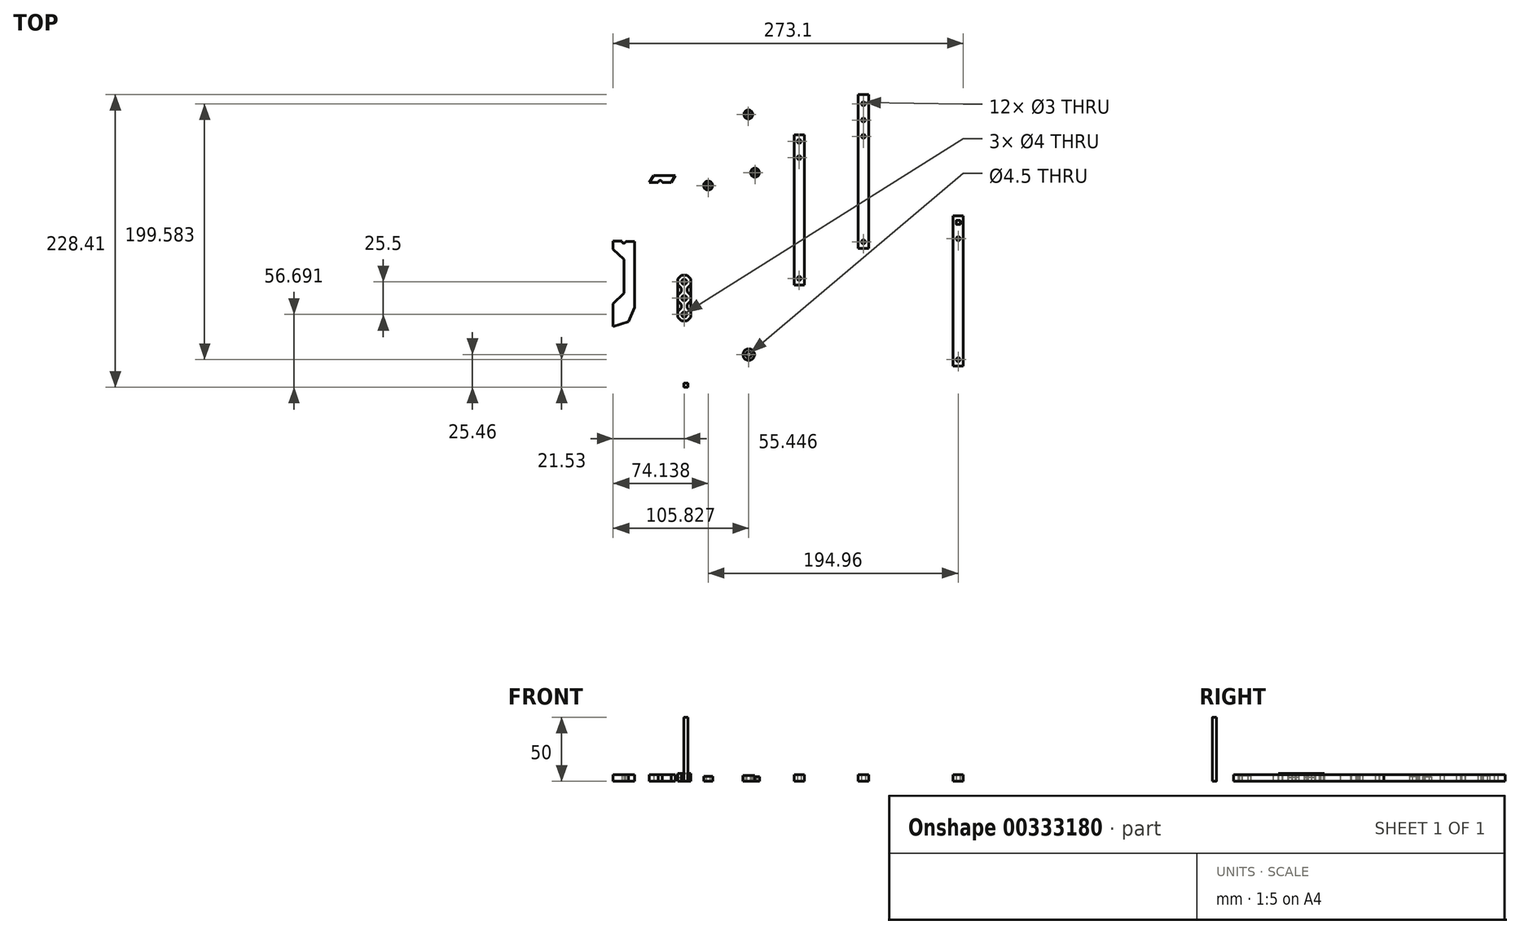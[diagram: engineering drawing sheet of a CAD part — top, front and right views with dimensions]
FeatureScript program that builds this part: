
annotation { "Feature Type Name" : "Feature", "Feature Type Description" : "" }
export const myFeature = defineFeature(function(context is Context, id is Id, definition is map)
    precondition{}
    {
        {
            var Q0;
            Q0=qCreatedBy(makeId("Top.planeOp"),FACE);
            var sketch = newSketch(context, id + "F0", { "sketchPlane" : qUnion([Q0])});
            skLineSegment(sketch, "E0", {"start": v(-67.95, 43.9) * mm, "end": v(-50.95, 43.9) * mm});
            skLineSegment(sketch, "E1", {"start": v(-67.95, 43.9) * mm, "end": v(-99.55, -7.1) * mm});
            skLineSegment(sketch, "E2", {"start": v(-50.95, 43.9) * mm, "end": v(-82.81, -7.53) * mm});
            skLineSegment(sketch, "E3", {"start": v(-99.55, -7.1) * mm, "end": v(-99.55, -13.4) * mm});
            skLineSegment(sketch, "E4", {"start": v(-82.81, -7.53) * mm, "end": v(-82.81, -59.03) * mm});
            skLineSegment(sketch, "E5", {"start": v(-82.81, -59.03) * mm, "end": v(-87.58, -70.04) * mm});
            skLineSegment(sketch, "E6", {"start": v(-87.58, -70.04) * mm, "end": v(-99.57, -73.9) * mm});
            skLineSegment(sketch, "E7", {"start": v(-99.57, -73.9) * mm, "end": v(-99.57, -55.9) * mm});
            skLineSegment(sketch, "E8", {"start": v(-99.55, -13.4) * mm, "end": v(-90.95, -13.4) * mm});
            skLineSegment(sketch, "E9", {"start": v(-90.95, -13.4) * mm, "end": v(-90.95, -55.9) * mm});
            skLineSegment(sketch, "E10", {"start": v(-90.95, -55.9) * mm, "end": v(-99.57, -55.9) * mm});
            skLineSegment(sketch, "E11", {"start": v(-99.55, -13.4) * mm, "end": v(-90.95, -21.4) * mm});
            skLineSegment(sketch, "E12", {"start": v(-99.57, -55.9) * mm, "end": v(-90.95, -47.88) * mm});
            skLineSegment(sketch, "E13", {"start": v(-99.55, -7.1) * mm, "end": v(-82.81, -7.53) * mm});
            skCircle(sketch, "E14", {"center": v(-91.18, -7.32) * mm, "radius": 1.5 * mm});
            skLineSegment(sketch, "E15", {"start": v(-71.24, 38.6) * mm, "end": v(-54.24, 38.6) * mm});
            skCircle(sketch, "E16", {"center": v(-62.74, 38.6) * mm, "radius": 1.5 * mm});
            skLineSegment(sketch, "E17", {"start": v(45.58, 70.63) * mm, "end": v(45.58, -36.33) * mm});
            skCircle(sketch, "E18", {"center": v(45.58, 70.63) * mm, "radius": 1.5 * mm});
            skCircle(sketch, "E19", {"center": v(45.58, -36.33) * mm, "radius": 1.5 * mm});
            skLineSegment(sketch, "E20.bottom", {"start": v(49.58, 75.65) * mm, "end": v(41.58, 75.65) * mm});
            skLineSegment(sketch, "E20.top", {"start": v(49.58, -41.35) * mm, "end": v(41.58, -41.35) * mm});
            skLineSegment(sketch, "E20.left", {"start": v(49.58, 75.65) * mm, "end": v(49.58, -41.35) * mm});
            skLineSegment(sketch, "E20.right", {"start": v(41.58, 75.65) * mm, "end": v(41.58, -41.35) * mm});
            skPoint(sketch, "E20.middle", {"position": v(45.58, 17.15) * mm});
            skLineSegment(sketch, "E21", {"start": v(95.66, 87.27) * mm, "end": v(95.66, -7.73) * mm});
            skCircle(sketch, "E22", {"center": v(95.66, 87.27) * mm, "radius": 1.5 * mm});
            skCircle(sketch, "E23", {"center": v(95.66, -7.73) * mm, "radius": 1.5 * mm});
            skLineSegment(sketch, "E24.bottom", {"start": v(99.66, 92.27) * mm, "end": v(91.66, 92.27) * mm});
            skLineSegment(sketch, "E24.top", {"start": v(99.66, -12.73) * mm, "end": v(91.66, -12.73) * mm});
            skLineSegment(sketch, "E24.left", {"start": v(99.66, 92.27) * mm, "end": v(99.66, -12.73) * mm});
            skLineSegment(sketch, "E24.right", {"start": v(91.66, 92.27) * mm, "end": v(91.66, -12.73) * mm});
            skPoint(sketch, "E24.middle", {"position": v(95.66, 39.77) * mm});
            skCircle(sketch, "E25", {"center": v(-42.75, -119.57) * mm, "radius": 1.5 * mm});
            skCircle(sketch, "E26", {"center": v(5.9, 91.64) * mm, "radius": 1.5 * mm});
            skCircle(sketch, "E27", {"center": v(5.9, 91.64) * mm, "radius": 3.5 * mm});
            skCircle(sketch, "E28", {"center": v(29.29, -65.49) * mm, "radius": 3.14 * mm});
            skLineSegment(sketch, "E29", {"start": v(169.53, -99.61) * mm, "end": v(169.53, 7.39) * mm});
            skLineSegment(sketch, "E30.bottom", {"start": v(173.53, 12.39) * mm, "end": v(165.53, 12.39) * mm});
            skLineSegment(sketch, "E30.top", {"start": v(173.53, -104.61) * mm, "end": v(165.53, -104.61) * mm});
            skLineSegment(sketch, "E30.left", {"start": v(173.53, 12.39) * mm, "end": v(173.53, -104.61) * mm});
            skLineSegment(sketch, "E30.right", {"start": v(165.53, 12.39) * mm, "end": v(165.53, -104.61) * mm});
            skPoint(sketch, "E30.middle", {"position": v(169.53, -46.11) * mm});
            skLineSegment(sketch, "E31.bottom", {"start": v(171.13, 8.99) * mm, "end": v(167.93, 8.99) * mm});
            skLineSegment(sketch, "E31.top", {"start": v(171.13, 5.79) * mm, "end": v(167.93, 5.79) * mm});
            skLineSegment(sketch, "E31.left", {"start": v(171.13, 8.99) * mm, "end": v(171.13, 5.79) * mm});
            skLineSegment(sketch, "E31.right", {"start": v(167.93, 8.99) * mm, "end": v(167.93, 5.79) * mm});
            skPoint(sketch, "E31.middle", {"position": v(169.53, 7.39) * mm});
            skCircle(sketch, "E32", {"center": v(169.53, -99.61) * mm, "radius": 1.5 * mm});
            skLineSegment(sketch, "E33.bottom", {"start": v(-41.18, -121.14) * mm, "end": v(-44.33, -121.14) * mm});
            skLineSegment(sketch, "E33.top", {"start": v(-41.18, -118) * mm, "end": v(-44.33, -118) * mm});
            skLineSegment(sketch, "E33.left", {"start": v(-41.18, -121.14) * mm, "end": v(-41.18, -118) * mm});
            skLineSegment(sketch, "E33.right", {"start": v(-44.33, -121.14) * mm, "end": v(-44.33, -118) * mm});
            skCircle(sketch, "E34", {"center": v(169.53, 7.39) * mm, "radius": 2.1 * mm});
            skLineSegment(sketch, "E35.bottom", {"start": v(165.53, 12.39) * mm, "end": v(173.53, 12.39) * mm});
            skLineSegment(sketch, "E35.top", {"start": v(165.53, 27.39) * mm, "end": v(173.53, 27.39) * mm});
            skLineSegment(sketch, "E35.left", {"start": v(165.53, 12.39) * mm, "end": v(165.53, 27.39) * mm});
            skLineSegment(sketch, "E35.right", {"start": v(173.53, 12.39) * mm, "end": v(173.53, 27.39) * mm});
            skCircle(sketch, "E36", {"center": v(169.53, 20.09) * mm, "radius": 1.5 * mm});
            skPoint(sketch, "E36.centerSnap0", {"position": v(169.53, 12.39) * mm});
            skCircle(sketch, "E37", {"center": v(169.53, -5.31) * mm, "radius": 1.5 * mm});
            skLineSegment(sketch, "E38.bottom", {"start": v(41.58, 75.65) * mm, "end": v(49.58, 75.65) * mm});
            skLineSegment(sketch, "E38.top", {"start": v(41.58, 90.65) * mm, "end": v(49.58, 90.65) * mm});
            skLineSegment(sketch, "E38.left", {"start": v(41.58, 75.65) * mm, "end": v(41.58, 90.65) * mm});
            skLineSegment(sketch, "E38.right", {"start": v(49.58, 75.65) * mm, "end": v(49.58, 90.65) * mm});
            skCircle(sketch, "E39", {"center": v(45.58, 83.33) * mm, "radius": 1.5 * mm});
            skPoint(sketch, "E39.centerSnap0", {"position": v(45.58, 75.65) * mm});
            skCircle(sketch, "E40", {"center": v(45.58, 57.93) * mm, "radius": 1.5 * mm});
            skLineSegment(sketch, "E41", {"start": v(91.66, 92.27) * mm, "end": v(91.66, 107.27) * mm});
            skLineSegment(sketch, "E42", {"start": v(91.66, 107.27) * mm, "end": v(99.66, 107.27) * mm});
            skLineSegment(sketch, "E43", {"start": v(99.66, 107.27) * mm, "end": v(99.66, 92.27) * mm});
            skCircle(sketch, "E44", {"center": v(95.66, 99.97) * mm, "radius": 1.5 * mm});
            skCircle(sketch, "E45", {"center": v(95.66, 74.57) * mm, "radius": 1.5 * mm});
            skCircle(sketch, "E46", {"center": v(6.26, -95.68) * mm, "radius": 2.25 * mm});
            skCircle(sketch, "E47", {"center": v(6.26, -95.68) * mm, "radius": 4.5 * mm});
            skSolve(sketch);
        }
        {
            var Q0;
            Q0=makeQuery(id+"F0.imprint","IMPRINT",FACE,{"disambiguationData":[TD([[makeQuery(id+"F0.imprint","IMPRINT",EDGE,{"derivedFrom":sQuery(id+"F0.wireOp",EDGE,"E0")}),-1.0]])]});
            var Q1;
            {var subQ0=sQuery(id+"F0.wireOp",EDGE,"E8");Q1=makeQuery(id+"F0.imprint","IMPRINT",FACE,{"disambiguationData":[TD([[makeQuery(id+"F0.imprint","IMPRINT",EDGE,{"derivedFrom":subQ0}),-1.0]])]});}
            var Q2;
            {var subQ0=sQuery(id+"F0.wireOp",EDGE,"E10");Q2=makeQuery(id+"F0.imprint","IMPRINT",FACE,{"disambiguationData":[TD([[makeQuery(id+"F0.imprint","IMPRINT",EDGE,{"derivedFrom":subQ0}),-1.0]])]});}
            var Q3;
            {var subQ0=sQuery(id+"F0.wireOp",EDGE,"E13");var subQ3=sQuery(id+"F0.wireOp",EDGE,"E14");var subQ12=makeQuery(id+"F0.imprint","INTERSECT",VERTEX,{"disambiguationData":[OD(0.0)],"derivedFrom":[subQ0,subQ3]});Q3=makeQuery(id+"F0.imprint","IMPRINT",FACE,{"disambiguationData":[TD([[makeQuery(id+"F0.imprint","IMPRINT",EDGE,{"disambiguationData":[TD([[subQ12,1.0]])],"derivedFrom":subQ3}),-1.0]])]});}
            var Q4;
            {var subQ5=sQuery(id+"F0.wireOp",EDGE,"E3");Q4=makeQuery(id+"F0.imprint","IMPRINT",FACE,{"disambiguationData":[TD([[makeQuery(id+"F0.imprint","IMPRINT",EDGE,{"derivedFrom":subQ5}),1.0]])]});}
            var Q5;
            Q5=makeQuery(id+"F0.imprint","IMPRINT",FACE,{"disambiguationData":[TD([[makeQuery(id+"F0.imprint","IMPRINT",EDGE,{"derivedFrom":sQuery(id+"F0.wireOp",EDGE,"E18")}),-1.0]])]});
            var Q6;
            Q6=makeQuery(id+"F0.imprint","IMPRINT",FACE,{"disambiguationData":[TD([[makeQuery(id+"F0.imprint","IMPRINT",EDGE,{"derivedFrom":sQuery(id+"F0.wireOp",EDGE,"E22")}),-1.0]])]});
            var Q7;
            {var subQ0=sQuery(id+"F0.wireOp",EDGE,"E34");var subQ1=sQuery(id+"F0.wireOp",EDGE,"E31.bottom");var subQ2=makeQuery(id+"F0.imprint","INTERSECT",VERTEX,{"disambiguationData":[OD(0.0)],"derivedFrom":[subQ1,subQ0]});Q7=makeQuery(id+"F0.imprint","IMPRINT",FACE,{"disambiguationData":[TD([[makeQuery(id+"F0.imprint","IMPRINT",EDGE,{"disambiguationData":[TD([[subQ2,-1.0]])],"derivedFrom":subQ1}),-1.0]])]});}
            var Q8;
            {var subQ0=sQuery(id+"F0.wireOp",EDGE,"E34");var subQ1=sQuery(id+"F0.wireOp",EDGE,"E31.right");var subQ2=makeQuery(id+"F0.imprint","INTERSECT",VERTEX,{"disambiguationData":[OD(0.0)],"derivedFrom":[subQ1,subQ0]});Q8=makeQuery(id+"F0.imprint","IMPRINT",FACE,{"disambiguationData":[TD([[makeQuery(id+"F0.imprint","IMPRINT",EDGE,{"disambiguationData":[TD([[subQ2,-1.0]])],"derivedFrom":subQ1}),-1.0]])]});}
            var Q9;
            {var subQ0=sQuery(id+"F0.wireOp",EDGE,"E34");var subQ1=sQuery(id+"F0.wireOp",EDGE,"E31.left");var subQ2=makeQuery(id+"F0.imprint","INTERSECT",VERTEX,{"disambiguationData":[OD(0.0)],"derivedFrom":[subQ1,subQ0]});Q9=makeQuery(id+"F0.imprint","IMPRINT",FACE,{"disambiguationData":[TD([[makeQuery(id+"F0.imprint","IMPRINT",EDGE,{"disambiguationData":[TD([[subQ2,-1.0]])],"derivedFrom":subQ1}),1.0]])]});}
            var Q10;
            {var subQ0=sQuery(id+"F0.wireOp",EDGE,"E31.top");var subQ1=sQuery(id+"F0.wireOp",EDGE,"E29");var subQ2=makeQuery(id+"F0.imprint","INTERSECT",VERTEX,{"derivedFrom":[subQ1,subQ0]});Q10=makeQuery(id+"F0.imprint","IMPRINT",FACE,{"disambiguationData":[TD([[makeQuery(id+"F0.imprint","IMPRINT",EDGE,{"disambiguationData":[TD([[subQ2,1.0]])],"derivedFrom":subQ1}),-1.0]])]});}
            var Q11;
            {var subQ0=sQuery(id+"F0.wireOp",EDGE,"E31.top");var subQ1=sQuery(id+"F0.wireOp",EDGE,"E29");var subQ2=makeQuery(id+"F0.imprint","INTERSECT",VERTEX,{"derivedFrom":[subQ1,subQ0]});Q11=makeQuery(id+"F0.imprint","IMPRINT",FACE,{"disambiguationData":[TD([[makeQuery(id+"F0.imprint","IMPRINT",EDGE,{"disambiguationData":[TD([[subQ2,1.0]])],"derivedFrom":subQ1}),1.0]])]});}
            var Q12;
            Q12=makeQuery(id+"F0.imprint","IMPRINT",FACE,{"disambiguationData":[TD([[makeQuery(id+"F0.imprint","IMPRINT",EDGE,{"derivedFrom":sQuery(id+"F0.wireOp",EDGE,"E30.bottom")}),1.0]])]});
            var Q13;
            {var subQ0=sQuery(id+"F0.wireOp",EDGE,"E31.left");var subQ1=sQuery(id+"F0.wireOp",EDGE,"E31.bottom");var subQ2=makeQuery(id+"F0.imprint","INTERSECT",VERTEX,{"derivedFrom":[subQ1,subQ0]});Q13=makeQuery(id+"F0.imprint","IMPRINT",FACE,{"disambiguationData":[TD([[makeQuery(id+"F0.imprint","IMPRINT",EDGE,{"disambiguationData":[TD([[subQ2,-1.0]])],"derivedFrom":subQ1}),1.0]])]});}
            var Q14;
            {var subQ0=sQuery(id+"F0.wireOp",EDGE,"E31.right");var subQ1=sQuery(id+"F0.wireOp",EDGE,"E31.bottom");var subQ2=makeQuery(id+"F0.imprint","INTERSECT",VERTEX,{"derivedFrom":[subQ1,subQ0]});Q14=makeQuery(id+"F0.imprint","IMPRINT",FACE,{"disambiguationData":[TD([[makeQuery(id+"F0.imprint","IMPRINT",EDGE,{"disambiguationData":[TD([[subQ2,1.0]])],"derivedFrom":subQ1}),1.0]])]});}
            var Q15;
            {var subQ0=sQuery(id+"F0.wireOp",EDGE,"E31.right");var subQ1=sQuery(id+"F0.wireOp",EDGE,"E31.top");var subQ2=makeQuery(id+"F0.imprint","INTERSECT",VERTEX,{"derivedFrom":[subQ1,subQ0]});Q15=makeQuery(id+"F0.imprint","IMPRINT",FACE,{"disambiguationData":[TD([[makeQuery(id+"F0.imprint","IMPRINT",EDGE,{"disambiguationData":[TD([[subQ2,1.0]])],"derivedFrom":subQ1}),-1.0]])]});}
            var Q16;
            {var subQ0=sQuery(id+"F0.wireOp",EDGE,"E31.left");var subQ1=sQuery(id+"F0.wireOp",EDGE,"E31.top");var subQ2=makeQuery(id+"F0.imprint","INTERSECT",VERTEX,{"derivedFrom":[subQ1,subQ0]});Q16=makeQuery(id+"F0.imprint","IMPRINT",FACE,{"disambiguationData":[TD([[makeQuery(id+"F0.imprint","IMPRINT",EDGE,{"disambiguationData":[TD([[subQ2,-1.0]])],"derivedFrom":subQ1}),-1.0]])]});}
            var Q17;
            Q17=makeQuery(id+"F0.imprint","IMPRINT",FACE,{"disambiguationData":[TD([[makeQuery(id+"F0.imprint","IMPRINT",EDGE,{"derivedFrom":sQuery(id+"F0.wireOp",EDGE,"E35.bottom")}),1.0]])]});
            var Q18;
            Q18=makeQuery(id+"F0.imprint","IMPRINT",FACE,{"disambiguationData":[TD([[makeQuery(id+"F0.imprint","IMPRINT",EDGE,{"derivedFrom":sQuery(id+"F0.wireOp",EDGE,"E30.top")}),-1.0]])]});
            var Q19;
            Q19=makeQuery(id+"F0.imprint","IMPRINT",FACE,{"disambiguationData":[TD([[makeQuery(id+"F0.imprint","IMPRINT",EDGE,{"derivedFrom":sQuery(id+"F0.wireOp",EDGE,"E38.bottom")}),1.0]])]});
            var Q20;
            Q20=makeQuery(id+"F0.imprint","IMPRINT",FACE,{"disambiguationData":[TD([[makeQuery(id+"F0.imprint","IMPRINT",EDGE,{"derivedFrom":sQuery(id+"F0.wireOp",EDGE,"E24.bottom")}),-1.0]])]});
            extrude(context, id + "F1", {"entities" : qUnion([Q0, Q1, Q2, Q3, Q4, Q5, Q6, Q7, Q8, Q9, Q10, Q11, Q12, Q13, Q14, Q15, Q16, Q17, Q18, Q19, Q20]), "depth" : 5.08 * mm});
        }
        {
            var Q0;
            Q0=makeQuery(id+"F0.imprint","IMPRINT",FACE,{"disambiguationData":[TD([[makeQuery(id+"F0.imprint","IMPRINT",EDGE,{"derivedFrom":sQuery(id+"F0.wireOp",EDGE,"E25")}),1.0]])]});
            var Q1;
            Q1=makeQuery(id+"F0.imprint","IMPRINT",FACE,{"disambiguationData":[TD([[makeQuery(id+"F0.imprint","IMPRINT",EDGE,{"derivedFrom":sQuery(id+"F0.wireOp",EDGE,"E25")}),-1.0]])]});
            extrude(context, id + "F2", {"entities" : qUnion([Q0, Q1]), "depth" : 50 * mm});
        }
        {
            var Q0;
            Q0=makeQuery(id+"F0.imprint","IMPRINT",FACE,{"disambiguationData":[TD([[makeQuery(id+"F0.imprint","IMPRINT",EDGE,{"derivedFrom":sQuery(id+"F0.wireOp",EDGE,"E26")}),-1.0]])]});
            var Q1;
            Q1=qSketchRegion(id+"F5",true);
            var Q2;
            Q2=makeQuery(id+"F0.imprint","IMPRINT",FACE,{"disambiguationData":[TD([[makeQuery(id+"F0.imprint","IMPRINT",EDGE,{"derivedFrom":sQuery(id+"F0.wireOp",EDGE,"E46")}),-1.0]])]});
            extrude(context, id + "F3", {"entities" : qUnion([Q0, Q1, Q2]), "depth" : 4.45 * mm});
        }
        {
            var Q0;
            Q0=makeQuery(id+"F2.opExtrude","SWEPT_EDGE",EDGE,{"disambiguationData":[OSD([sQuery(id+"F0.wireOp",EDGE,"E33.bottom"),sQuery(id+"F0.wireOp",EDGE,"E33.left")])]});
            var Q1;
            Q1=makeQuery(id+"F2.opExtrude","SWEPT_EDGE",EDGE,{"disambiguationData":[OSD([sQuery(id+"F0.wireOp",EDGE,"E33.top"),sQuery(id+"F0.wireOp",EDGE,"E33.right")])]});
            var Q2;
            Q2=makeQuery(id+"F2.opExtrude","SWEPT_EDGE",EDGE,{"disambiguationData":[OSD([sQuery(id+"F0.wireOp",EDGE,"E33.bottom"),sQuery(id+"F0.wireOp",EDGE,"E33.right")])]});
            var Q3;
            Q3=makeQuery(id+"F2.opExtrude","SWEPT_EDGE",EDGE,{"disambiguationData":[OSD([sQuery(id+"F0.wireOp",EDGE,"E33.top"),sQuery(id+"F0.wireOp",EDGE,"E33.left")])]});
            fillet(context, id + "F4", {"entities" : qUnion([Q0, Q1, Q2, Q3]), "radius" : 0.25 * mm, "tangentPropagation" : true, "allowEdgeOverflow" : false});
        }
        {
            var Q0;
            Q0=qCreatedBy(makeId("Top.planeOp"),FACE);
            var sketch = newSketch(context, id + "F5", { "sketchPlane" : qUnion([Q0])});
            skCircle(sketch, "E48", {"center": v(-25.43, 36.16) * mm, "radius": 3.5 * mm});
            skCircle(sketch, "E49", {"center": v(-25.43, 36.16) * mm, "radius": 1.5 * mm});
            skCircle(sketch, "E50", {"center": v(11.1, 46.21) * mm, "radius": 3.5 * mm});
            skCircle(sketch, "E51", {"center": v(11.1, 46.21) * mm, "radius": 1.5 * mm});
            skSolve(sketch);
        }
        {
            var Q0;
            Q0=makeQuery(id+"F5.imprint","IMPRINT",FACE,{"disambiguationData":[TD([[makeQuery(id+"F5.imprint","IMPRINT",EDGE,{"derivedFrom":sQuery(id+"F5.wireOp",EDGE,"E48")}),1.0]])]});
            extrude(context, id + "F6", {"entities" : qUnion([Q0]), "depth" : 3.81 * mm});
        }
        {
            var Q0;
            Q0=qCreatedBy(makeId("Top.planeOp"),FACE);
            var sketch = newSketch(context, id + "F7", { "sketchPlane" : qUnion([Q0])});
            skCircle(sketch, "E52", {"center": v(-44.12, -38.95) * mm, "radius": 2 * mm});
            skCircle(sketch, "E53", {"center": v(-44.12, -51.7) * mm, "radius": 2 * mm});
            skCircle(sketch, "E54", {"center": v(-44.12, -64.45) * mm, "radius": 2 * mm});
            skLineSegment(sketch, "E55", {"start": v(-44.12, -51.7) * mm, "end": v(-44.12, -38.95) * mm});
            skLineSegment(sketch, "E56", {"start": v(-44.12, -51.7) * mm, "end": v(-44.12, -64.45) * mm});
            skLineSegment(sketch, "E57", {"start": v(-46.37, -33.85) * mm, "end": v(-41.87, -33.85) * mm});
            skLineSegment(sketch, "E58", {"start": v(-49.22, -41.2) * mm, "end": v(-49.22, -36.7) * mm});
            skLineSegment(sketch, "E59.MirrorCS", {"start": v(-39.02, -41.2) * mm, "end": v(-39.02, -36.7) * mm});
            skLineSegment(sketch, "E60", {"start": v(-49.22, -36.7) * mm, "end": v(-46.37, -33.85) * mm});
            skLineSegment(sketch, "E61", {"start": v(-41.87, -33.85) * mm, "end": v(-39.02, -36.7) * mm});
            skLineSegment(sketch, "E62", {"start": v(-44.12, -38.95) * mm, "end": v(-39.02, -38.95) * mm});
            skPoint(sketch, "E62.endSnap0", {"position": v(-39.02, -38.94) * mm});
            skLineSegment(sketch, "E63.MirrorCS", {"start": v(-46.37, -44.05) * mm, "end": v(-41.87, -44.05) * mm});
            skLineSegment(sketch, "E64", {"start": v(-49.22, -41.2) * mm, "end": v(-46.37, -44.05) * mm});
            skLineSegment(sketch, "E65", {"start": v(-41.87, -44.05) * mm, "end": v(-39.02, -41.2) * mm});
            skPoint(sketch, "E66.endSnap0", {"position": v(-44.12, -45.32) * mm});
            skLineSegment(sketch, "E67.MirrorCS", {"start": v(-46.37, -46.6) * mm, "end": v(-41.87, -46.6) * mm});
            skLineSegment(sketch, "E68.MirrorCS", {"start": v(-41.87, -46.6) * mm, "end": v(-39.02, -49.46) * mm});
            skLineSegment(sketch, "E69.MirrorCS", {"start": v(-49.22, -49.46) * mm, "end": v(-46.37, -46.6) * mm});
            skLineSegment(sketch, "E70.MirrorCS", {"start": v(-49.22, -49.46) * mm, "end": v(-49.22, -53.96) * mm});
            skLineSegment(sketch, "E71.MirrorCS", {"start": v(-49.22, -53.96) * mm, "end": v(-46.37, -56.8) * mm});
            skLineSegment(sketch, "E72.MirrorCS", {"start": v(-46.37, -56.8) * mm, "end": v(-41.87, -56.8) * mm});
            skLineSegment(sketch, "E73.MirrorCS", {"start": v(-41.87, -56.8) * mm, "end": v(-39.02, -53.96) * mm});
            skLineSegment(sketch, "E74.MirrorCS", {"start": v(-39.02, -49.46) * mm, "end": v(-39.02, -53.96) * mm});
            skLineSegment(sketch, "E75.MirrorCS", {"start": v(-46.37, -59.35) * mm, "end": v(-41.87, -59.35) * mm});
            skLineSegment(sketch, "E76.MirrorCS", {"start": v(-41.87, -59.35) * mm, "end": v(-39.02, -62.2) * mm});
            skLineSegment(sketch, "E77.MirrorCS", {"start": v(-39.02, -66.7) * mm, "end": v(-39.02, -62.2) * mm});
            skLineSegment(sketch, "E78.MirrorCS", {"start": v(-41.87, -69.55) * mm, "end": v(-39.02, -66.7) * mm});
            skLineSegment(sketch, "E79.MirrorCS", {"start": v(-49.22, -62.2) * mm, "end": v(-46.37, -59.35) * mm});
            skLineSegment(sketch, "E80.MirrorCS", {"start": v(-49.22, -66.7) * mm, "end": v(-49.22, -62.2) * mm});
            skLineSegment(sketch, "E81.MirrorCS", {"start": v(-49.22, -66.7) * mm, "end": v(-46.37, -69.55) * mm});
            skLineSegment(sketch, "E82.MirrorCS", {"start": v(-46.37, -69.55) * mm, "end": v(-41.87, -69.55) * mm});
            skLineSegment(sketch, "E83", {"start": v(-46.37, -46.6) * mm, "end": v(-46.37, -44.05) * mm});
            skLineSegment(sketch, "E84", {"start": v(-41.87, -44.05) * mm, "end": v(-41.87, -46.6) * mm});
            skLineSegment(sketch, "E85", {"start": v(-46.37, -56.8) * mm, "end": v(-46.37, -59.35) * mm});
            skLineSegment(sketch, "E86", {"start": v(-41.87, -56.8) * mm, "end": v(-41.87, -59.35) * mm});
            skLineSegment(sketch, "E87", {"start": v(-49.22, -49.46) * mm, "end": v(-49.22, -41.2) * mm});
            skLineSegment(sketch, "E88", {"start": v(-39.02, -41.2) * mm, "end": v(-39.02, -49.46) * mm});
            skLineSegment(sketch, "E89", {"start": v(-39.02, -53.96) * mm, "end": v(-39.02, -62.2) * mm});
            skLineSegment(sketch, "E90", {"start": v(-49.22, -53.96) * mm, "end": v(-49.22, -62.2) * mm});
            skSolve(sketch);
        }
        {
            var Q0;
            Q0=makeQuery(id+"F7.imprint","IMPRINT",FACE,{"disambiguationData":[TD([[makeQuery(id+"F7.imprint","IMPRINT",EDGE,{"derivedFrom":sQuery(id+"F7.wireOp",EDGE,"E65")}),-1.0]])]});
            var Q1;
            Q1=makeQuery(id+"F7.imprint","IMPRINT",FACE,{"disambiguationData":[TD([[makeQuery(id+"F7.imprint","IMPRINT",EDGE,{"derivedFrom":sQuery(id+"F7.wireOp",EDGE,"E64")}),-1.0]])]});
            var Q2;
            Q2=makeQuery(id+"F7.imprint","IMPRINT",FACE,{"disambiguationData":[TD([[makeQuery(id+"F7.imprint","IMPRINT",EDGE,{"derivedFrom":sQuery(id+"F7.wireOp",EDGE,"E71.MirrorCS")}),-1.0]])]});
            var Q3;
            Q3=makeQuery(id+"F7.imprint","IMPRINT",FACE,{"disambiguationData":[TD([[makeQuery(id+"F7.imprint","IMPRINT",EDGE,{"derivedFrom":sQuery(id+"F7.wireOp",EDGE,"E73.MirrorCS")}),-1.0]])]});
            extrude(context, id + "F8", {"entities" : qUnion([Q0, Q1, Q2, Q3]), "depth" : 3.1 * mm});
        }
        {
            var Q0;
            Q0=makeQuery(id+"F7.imprint","IMPRINT",FACE,{"disambiguationData":[TD([[makeQuery(id+"F7.imprint","IMPRINT",EDGE,{"derivedFrom":sQuery(id+"F7.wireOp",EDGE,"E57")}),-1.0]])]});
            var Q1;
            {var subQ5=sQuery(id+"F7.wireOp",EDGE,"E65");Q1=makeQuery(id+"F7.imprint","IMPRINT",FACE,{"disambiguationData":[TD([[makeQuery(id+"F7.imprint","IMPRINT",EDGE,{"derivedFrom":subQ5}),1.0]])]});}
            var Q2;
            {var subQ0=sQuery(id+"F7.wireOp",EDGE,"E68.MirrorCS");Q2=makeQuery(id+"F7.imprint","IMPRINT",FACE,{"disambiguationData":[TD([[makeQuery(id+"F7.imprint","IMPRINT",EDGE,{"derivedFrom":subQ0}),-1.0]])]});}
            var Q3;
            {var subQ0=sQuery(id+"F7.wireOp",EDGE,"E69.MirrorCS");Q3=makeQuery(id+"F7.imprint","IMPRINT",FACE,{"disambiguationData":[TD([[makeQuery(id+"F7.imprint","IMPRINT",EDGE,{"derivedFrom":subQ0}),-1.0]])]});}
            var Q4;
            Q4=makeQuery(id+"F7.imprint","IMPRINT",FACE,{"disambiguationData":[TD([[makeQuery(id+"F7.imprint","IMPRINT",EDGE,{"derivedFrom":sQuery(id+"F7.wireOp",EDGE,"E54")}),-1.0]])]});
            var Q5;
            {var subQ5=sQuery(id+"F7.wireOp",EDGE,"E83");Q5=makeQuery(id+"F7.imprint","IMPRINT",FACE,{"disambiguationData":[TD([[makeQuery(id+"F7.imprint","IMPRINT",EDGE,{"derivedFrom":subQ5}),-1.0]])]});}
            var Q6;
            {var subQ5=sQuery(id+"F7.wireOp",EDGE,"E84");Q6=makeQuery(id+"F7.imprint","IMPRINT",FACE,{"disambiguationData":[TD([[makeQuery(id+"F7.imprint","IMPRINT",EDGE,{"derivedFrom":subQ5}),-1.0]])]});}
            var Q7;
            {var subQ5=sQuery(id+"F7.wireOp",EDGE,"E85");Q7=makeQuery(id+"F7.imprint","IMPRINT",FACE,{"disambiguationData":[TD([[makeQuery(id+"F7.imprint","IMPRINT",EDGE,{"derivedFrom":subQ5}),1.0]])]});}
            var Q8;
            {var subQ5=sQuery(id+"F7.wireOp",EDGE,"E86");Q8=makeQuery(id+"F7.imprint","IMPRINT",FACE,{"disambiguationData":[TD([[makeQuery(id+"F7.imprint","IMPRINT",EDGE,{"derivedFrom":subQ5}),-1.0]])]});}
            extrude(context, id + "F9", {"entities" : qUnion([Q0, Q1, Q2, Q3, Q4, Q5, Q6, Q7, Q8]), "depth" : 6.15 * mm});
        }
        {
            var Q0;
            Q0=makeQuery(id+"F5.imprint","IMPRINT",FACE,{"disambiguationData":[TD([[makeQuery(id+"F5.imprint","IMPRINT",EDGE,{"derivedFrom":sQuery(id+"F5.wireOp",EDGE,"E50")}),1.0]])]});
            extrude(context, id + "F10", {"entities" : qUnion([Q0]), "depth" : 3.76 * mm});
        }
    });
